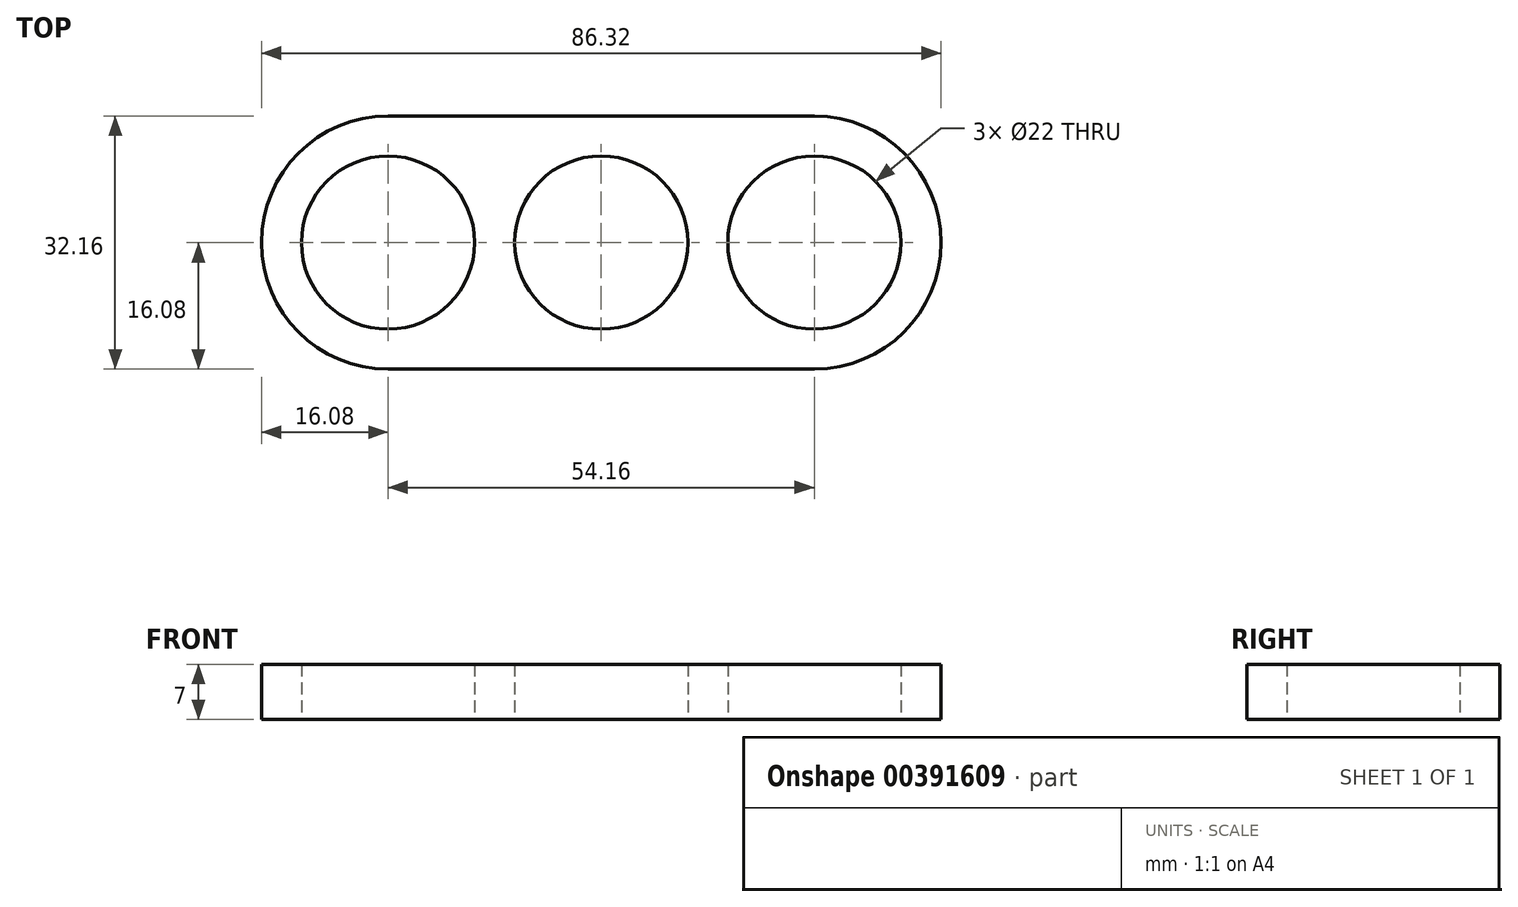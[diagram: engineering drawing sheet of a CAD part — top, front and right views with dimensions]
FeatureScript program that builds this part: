
annotation { "Feature Type Name" : "Feature", "Feature Type Description" : "" }
export const myFeature = defineFeature(function(context is Context, id is Id, definition is map)
    precondition{}
    {
        {
            var Q0;
            Q0=qCreatedBy(makeId("Top.planeOp"),FACE);
            var sketch = newSketch(context, id + "F0", { "sketchPlane" : qUnion([Q0])});
            skArc(sketch, "E0", {"start": v(0, 11) * mm, "mid": v(-11, 0) * mm, "end": v(0, -11) * mm});
            skCircle(sketch, "E1", {"center": v(-27.08, 0) * mm, "radius": 11 * mm});
            skPoint(sketch, "E2.orphan", {"position": v(-43.16, 16.08) * mm});
            skPoint(sketch, "E3.orphan", {"position": v(-43.16, -16.08) * mm});
            skPoint(sketch, "E4.start.orphan", {"position": v(-43.16, 0) * mm});
            skArc(sketch, "E5", {"start": v(-27.08, -16.08) * mm, "mid": v(-43.16, 0) * mm, "end": v(-27.08, 16.08) * mm});
            skPoint(sketch, "E6.orphan", {"position": v(-16.08, 0) * mm});
            skPoint(sketch, "E7.orphan", {"position": v(-11, 0) * mm});
            skCircle(sketch, "E8.MirrorC", {"center": v(27.08, 0) * mm, "radius": 11 * mm});
            skPoint(sketch, "E9.MirrorP", {"position": v(11, 0) * mm});
            skPoint(sketch, "E10.MirrorP", {"position": v(16.08, 0) * mm});
            skPoint(sketch, "E11.MirrorP", {"position": v(43.16, 16.08) * mm});
            skArc(sketch, "E12.MirrorCS", {"start": v(27.08, -16.08) * mm, "mid": v(43.16, 0) * mm, "end": v(27.08, 16.08) * mm});
            skArc(sketch, "E13.MirrorCS", {"start": v(0, 11) * mm, "mid": v(11, 0) * mm, "end": v(0, -11) * mm});
            skPoint(sketch, "E14.MirrorP", {"position": v(43.16, 0) * mm});
            skPoint(sketch, "E15.MirrorP", {"position": v(43.16, -16.08) * mm});
            skLineSegment(sketch, "E16", {"start": v(-27.08, 16.08) * mm, "end": v(27.08, 16.08) * mm});
            skLineSegment(sketch, "E17", {"start": v(-27.08, -16.08) * mm, "end": v(27.08, -16.08) * mm});
            skPoint(sketch, "E18.end.orphan", {"position": v(-13.54, 8.67) * mm});
            skPoint(sketch, "E18.start.orphan", {"position": v(0, 16.08) * mm});
            skPoint(sketch, "E19.MirrorCS.end.orphan", {"position": v(13.54, 8.67) * mm});
            skPoint(sketch, "E20.MirrorCS.start.orphan", {"position": v(0, -16.08) * mm});
            skPoint(sketch, "E21.MirrorCS.end.orphan", {"position": v(13.54, -8.67) * mm});
            skPoint(sketch, "E22.end.orphan", {"position": v(-13.54, -8.67) * mm});
            skSolve(sketch);
        }
        {
            var Q0;
            Q0=qSketchRegion(id+"F0",true);
            extrude(context, id + "F1", {"entities" : qUnion([Q0]), "depth" : 7 * mm});
        }
    });
